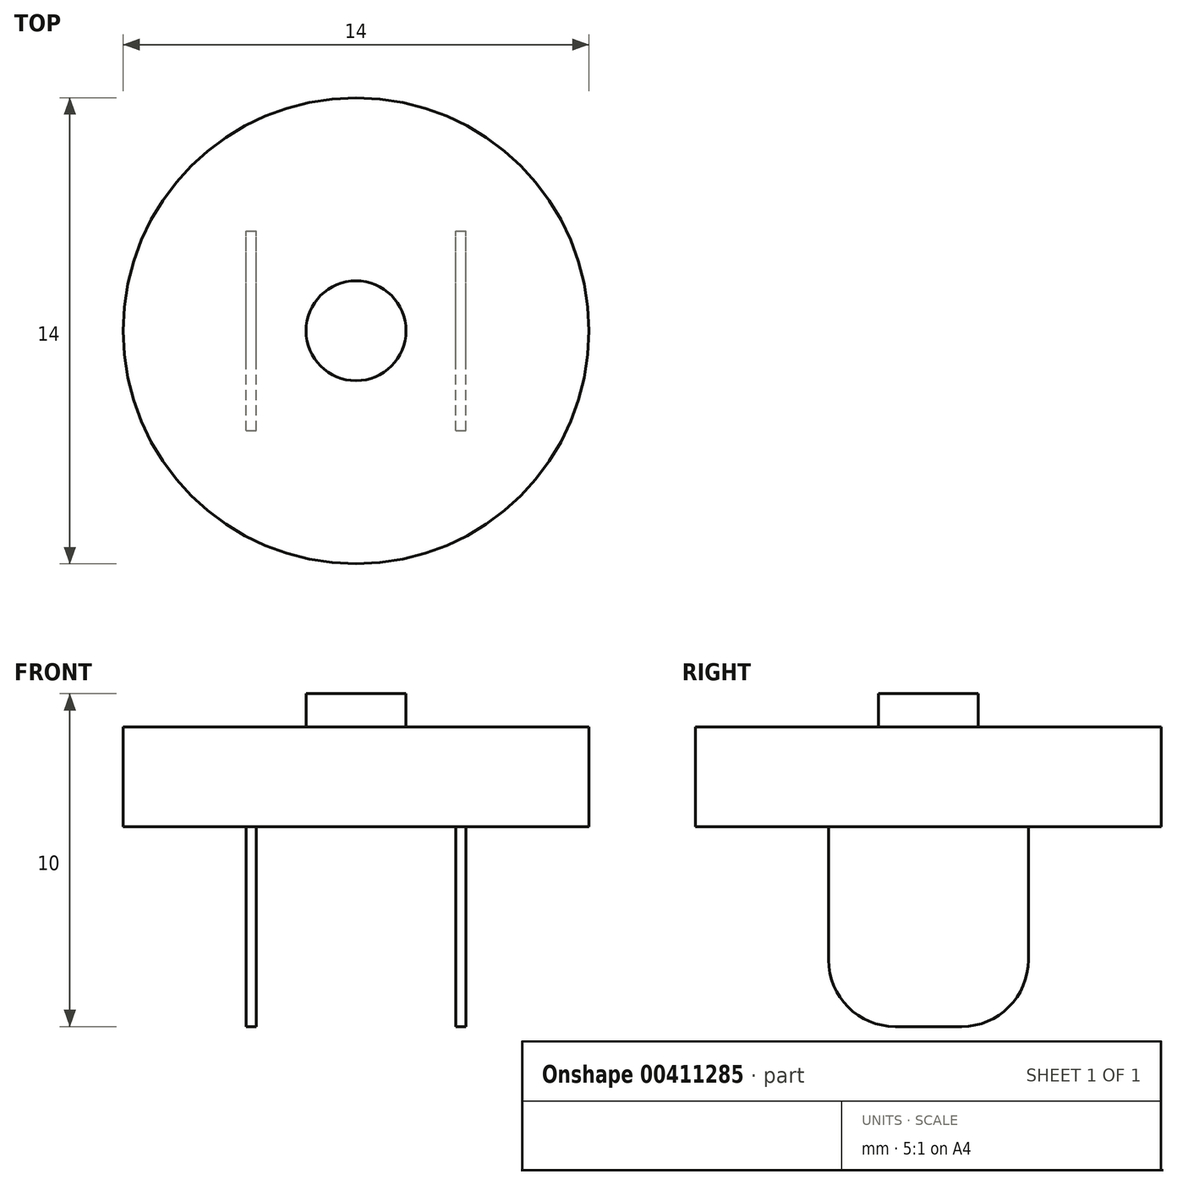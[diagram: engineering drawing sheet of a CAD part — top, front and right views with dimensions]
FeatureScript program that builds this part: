
annotation { "Feature Type Name" : "Feature", "Feature Type Description" : "" }
export const myFeature = defineFeature(function(context is Context, id is Id, definition is map)
    precondition{}
    {
        {
            var Q0;
            Q0=qCreatedBy(makeId("Top.planeOp"),FACE);
            var sketch = newSketch(context, id + "F0", { "sketchPlane" : qUnion([Q0])});
            skCircle(sketch, "E0", {"center": v(0, 0) * mm, "radius": 7 * mm});
            skCircle(sketch, "E1", {"center": v(0, 0) * mm, "radius": 1.5 * mm});
            skSolve(sketch);
        }
        {
            var Q0;
            Q0=qSketchRegion(id+"F0",true);
            extrude(context, id + "F1", {"entities" : qUnion([Q0]), "depth" : 3 * mm});
        }
        {
            var Q0;
            Q0=makeQuery(id+"F1.opExtrude","CAP_FACE",FACE,{"disambiguationData":[OSD([sQuery(id+"F0.wireOp",EDGE,"E0"),sQuery(id+"F0.wireOp",EDGE,"E1")])],"isStart":true});
            var sketch = newSketch(context, id + "F2", { "sketchPlane" : qUnion([Q0])});
            skCircle(sketch, "E2", {"center": v(0, 0) * mm, "radius": 1.55 * mm});
            skSolve(sketch);
        }
        {
            var Q0;
            Q0=qSketchRegion(id+"F2",true);
            extrude(context, id + "F3", {"entities" : qUnion([Q0]), "operationType" : NewBodyOperationType.ADD, "oppositeDirection" : true, "depth" : 1.5 * mm});
        }
        {
            var Q0;
            Q0=makeQuery(id+"F3.boolean.opBoolean","MERGE",FACE,{"derivedFrom":[makeQuery(id+"F1.opExtrude","CAP_FACE",FACE,{"disambiguationData":[OSD([sQuery(id+"F0.wireOp",EDGE,"E0"),sQuery(id+"F0.wireOp",EDGE,"E1")])],"isStart":true}),makeQuery(id+"F3.opExtrude","CAP_FACE",FACE,{"disambiguationData":[OSD([sQuery(id+"F2.wireOp",EDGE,"E2")])],"isStart":true})]});
            var sketch = newSketch(context, id + "F4", { "sketchPlane" : qUnion([Q0])});
            skLineSegment(sketch, "E3.bottom", {"start": v(-3.3, 3) * mm, "end": v(-3, 3) * mm});
            skLineSegment(sketch, "E3.top", {"start": v(-3.3, -3) * mm, "end": v(-3, -3) * mm});
            skLineSegment(sketch, "E3.left", {"start": v(-3.3, 3) * mm, "end": v(-3.3, -3) * mm});
            skLineSegment(sketch, "E3.right", {"start": v(-3, 3) * mm, "end": v(-3, -3) * mm});
            skLineSegment(sketch, "E4.bottom", {"start": v(3, 3) * mm, "end": v(3.3, 3) * mm});
            skLineSegment(sketch, "E4.top", {"start": v(3, -3) * mm, "end": v(3.3, -3) * mm});
            skLineSegment(sketch, "E4.left", {"start": v(3, 3) * mm, "end": v(3, -3) * mm});
            skLineSegment(sketch, "E4.right", {"start": v(3.3, 3) * mm, "end": v(3.3, -3) * mm});
            skSolve(sketch);
        }
        {
            var Q0;
            Q0=qSketchRegion(id+"F4",true);
            extrude(context, id + "F5", {"entities" : qUnion([Q0]), "operationType" : NewBodyOperationType.ADD, "depth" : 6 * mm});
        }
        {
            var Q0;
            Q0=makeQuery(id+"F5.opExtrude","CAP_EDGE",EDGE,{"disambiguationData":[OSD([sQuery(id+"F4.wireOp",EDGE,"E3.bottom")])],"isStart":false});
            var Q1;
            Q1=makeQuery(id+"F5.opExtrude","CAP_EDGE",EDGE,{"disambiguationData":[OSD([sQuery(id+"F4.wireOp",EDGE,"E3.top")])],"isStart":false});
            var Q2;
            Q2=makeQuery(id+"F5.opExtrude","CAP_EDGE",EDGE,{"disambiguationData":[OSD([sQuery(id+"F4.wireOp",EDGE,"E4.top")])],"isStart":false});
            var Q3;
            Q3=makeQuery(id+"F5.opExtrude","CAP_EDGE",EDGE,{"disambiguationData":[OSD([sQuery(id+"F4.wireOp",EDGE,"E4.bottom")])],"isStart":false});
            fillet(context, id + "F6", {"entities" : qUnion([Q0, Q1, Q2, Q3]), "radius" : 2 * mm, "tangentPropagation" : true, "allowEdgeOverflow" : false});
        }
        {
            var Q0;
            Q0=makeQuery(id+"F3.boolean.opBoolean","MERGE",FACE,{"derivedFrom":[makeQuery(id+"F1.opExtrude","CAP_FACE",FACE,{"disambiguationData":[OSD([sQuery(id+"F0.wireOp",EDGE,"E0"),sQuery(id+"F0.wireOp",EDGE,"E1")])],"isStart":true}),makeQuery(id+"F3.opExtrude","CAP_FACE",FACE,{"disambiguationData":[OSD([sQuery(id+"F2.wireOp",EDGE,"E2")])],"isStart":true})]});
            var sketch = newSketch(context, id + "F7", { "sketchPlane" : qUnion([Q0])});
            skCircle(sketch, "E5", {"center": v(0, 0) * mm, "radius": 1.5 * mm});
            skSolve(sketch);
        }
        {
            var Q0;
            Q0=makeQuery(id+"F7.imprint","IMPRINT",FACE,{"disambiguationData":[TD([[makeQuery(id+"F7.imprint","IMPRINT",EDGE,{"derivedFrom":sQuery(id+"F7.wireOp",EDGE,"E5")}),1.0]])]});
            extrude(context, id + "F8", {"entities" : qUnion([Q0]), "operationType" : NewBodyOperationType.ADD, "oppositeDirection" : true, "depth" : 4 * mm});
        }
    });
